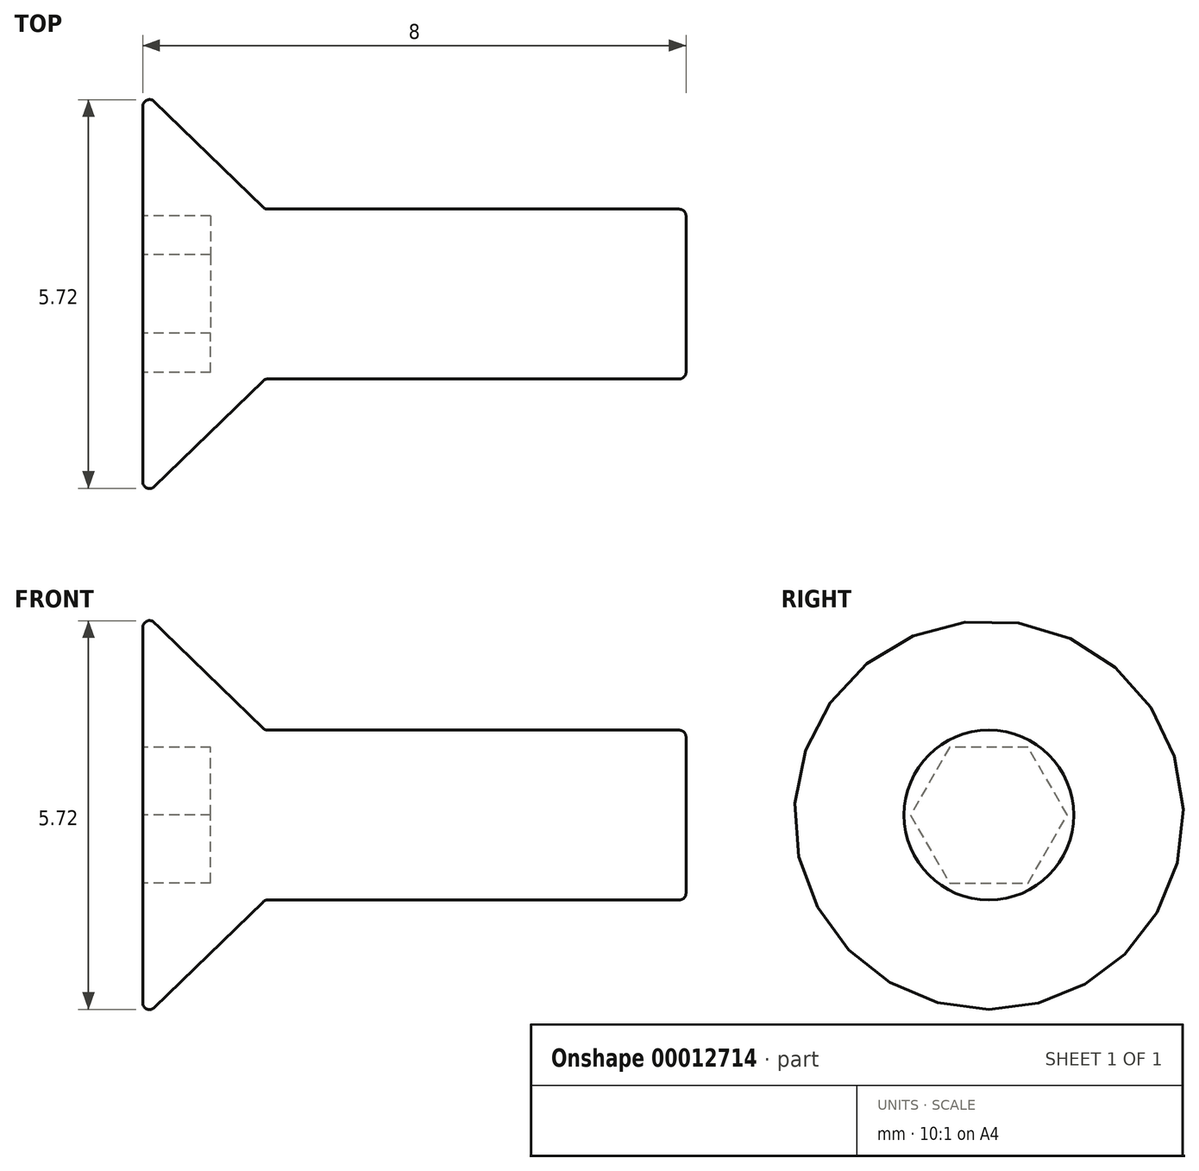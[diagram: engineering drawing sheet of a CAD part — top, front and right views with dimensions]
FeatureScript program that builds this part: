
annotation { "Feature Type Name" : "Feature", "Feature Type Description" : "" }
export const myFeature = defineFeature(function(context is Context, id is Id, definition is map)
    precondition{}
    {
        {
            var Q0;
            Q0=qCreatedBy(makeId("Top.planeOp"),FACE);
            var sketch = newSketch(context, id + "F0", { "sketchPlane" : qUnion([Q0])});
            skLineSegment(sketch, "E0", {"start": v(0, 0) * mm, "end": v(0, 3) * mm});
            skLineSegment(sketch, "E1", {"start": v(0, 3) * mm, "end": v(1.8, 1.25) * mm});
            skLineSegment(sketch, "E2", {"start": v(1.8, 1.25) * mm, "end": v(8, 1.25) * mm});
            skLineSegment(sketch, "E3", {"start": v(8, 1.25) * mm, "end": v(8, 0) * mm});
            skLineSegment(sketch, "E4", {"start": v(8, 0) * mm, "end": v(0, 0) * mm});
            skSolve(sketch);
        }
        {
            var Q0;
            Q0 = qSketchRegion(id + "F0", true);
            var Q1;
            Q1=sQuery(id+"F0.wireOp",EDGE,"E4");
            revolve(context, id + "F1", {"entities" : qUnion([Q0]), "axis" : qUnion([Q1]), "revolveType" : RevolveType.FULL});
        }
        {
            var Q0;
            Q0=makeQuery(id+"F1.opRevolve","SWEPT_EDGE",EDGE,{"disambiguationData":[OSD([sQuery(id+"F0.wireOp",EDGE,"E1"),sQuery(id+"F0.wireOp",EDGE,"E2")])]});
            var Q1;
            Q1=makeQuery(id+"F1.opRevolve","SWEPT_EDGE",EDGE,{"disambiguationData":[OSD([sQuery(id+"F0.wireOp",EDGE,"E2"),sQuery(id+"F0.wireOp",EDGE,"E3")])]});
            var Q2;
            Q2=makeQuery(id+"F1.opRevolve","SWEPT_EDGE",EDGE,{"disambiguationData":[OSD([sQuery(id+"F0.wireOp",EDGE,"E0"),sQuery(id+"F0.wireOp",EDGE,"E1")])]});
            fillet(context, id + "F2", {"entities" : qUnion([Q0, Q1, Q2]), "radius" : 0.1 * mm, "tangentPropagation" : true, "allowEdgeOverflow" : false});
        }
        {
            var Q0;
            Q0=makeQuery(id+"F1.opRevolve","SWEPT_FACE",FACE,{"disambiguationData":[OSD([sQuery(id+"F0.wireOp",EDGE,"E0")])]});
            var sketch = newSketch(context, id + "F3", { "sketchPlane" : qUnion([Q0])});
            skCircle(sketch, "E5", {"center": v(0, 0) * mm, "radius": 1 * mm, "construction": true});
            skLineSegment(sketch, "E6.0", {"start": v(-0.58, 1) * mm, "end": v(0.58, 1) * mm});
            skLineSegment(sketch, "E6.1", {"start": v(0.58, 1) * mm, "end": v(1.15, 0) * mm});
            skLineSegment(sketch, "E6.2", {"start": v(1.15, 0) * mm, "end": v(0.58, -1) * mm});
            skLineSegment(sketch, "E6.3", {"start": v(0.58, -1) * mm, "end": v(-0.58, -1) * mm});
            skLineSegment(sketch, "E6.4", {"start": v(-0.58, -1) * mm, "end": v(-1.15, 0) * mm});
            skLineSegment(sketch, "E6.5", {"start": v(-1.15, 0) * mm, "end": v(-0.58, 1) * mm});
            skPoint(sketch, "E6.0.midPoint", {"position": v(0, 1) * mm});
            skSolve(sketch);
        }
        {
            var Q0;
            Q0=makeQuery(id+"F3.imprint","IMPRINT",FACE,{"disambiguationData":[TD([[makeQuery(id+"F3.imprint","IMPRINT",EDGE,{"derivedFrom":sQuery(id+"F3.wireOp",EDGE,"E6.0")}),-1.0]])]});
            extrude(context, id + "F4", {"entities" : qUnion([Q0]), "operationType" : NewBodyOperationType.REMOVE, "oppositeDirection" : true, "depth" : 1 * mm});
        }
    });
